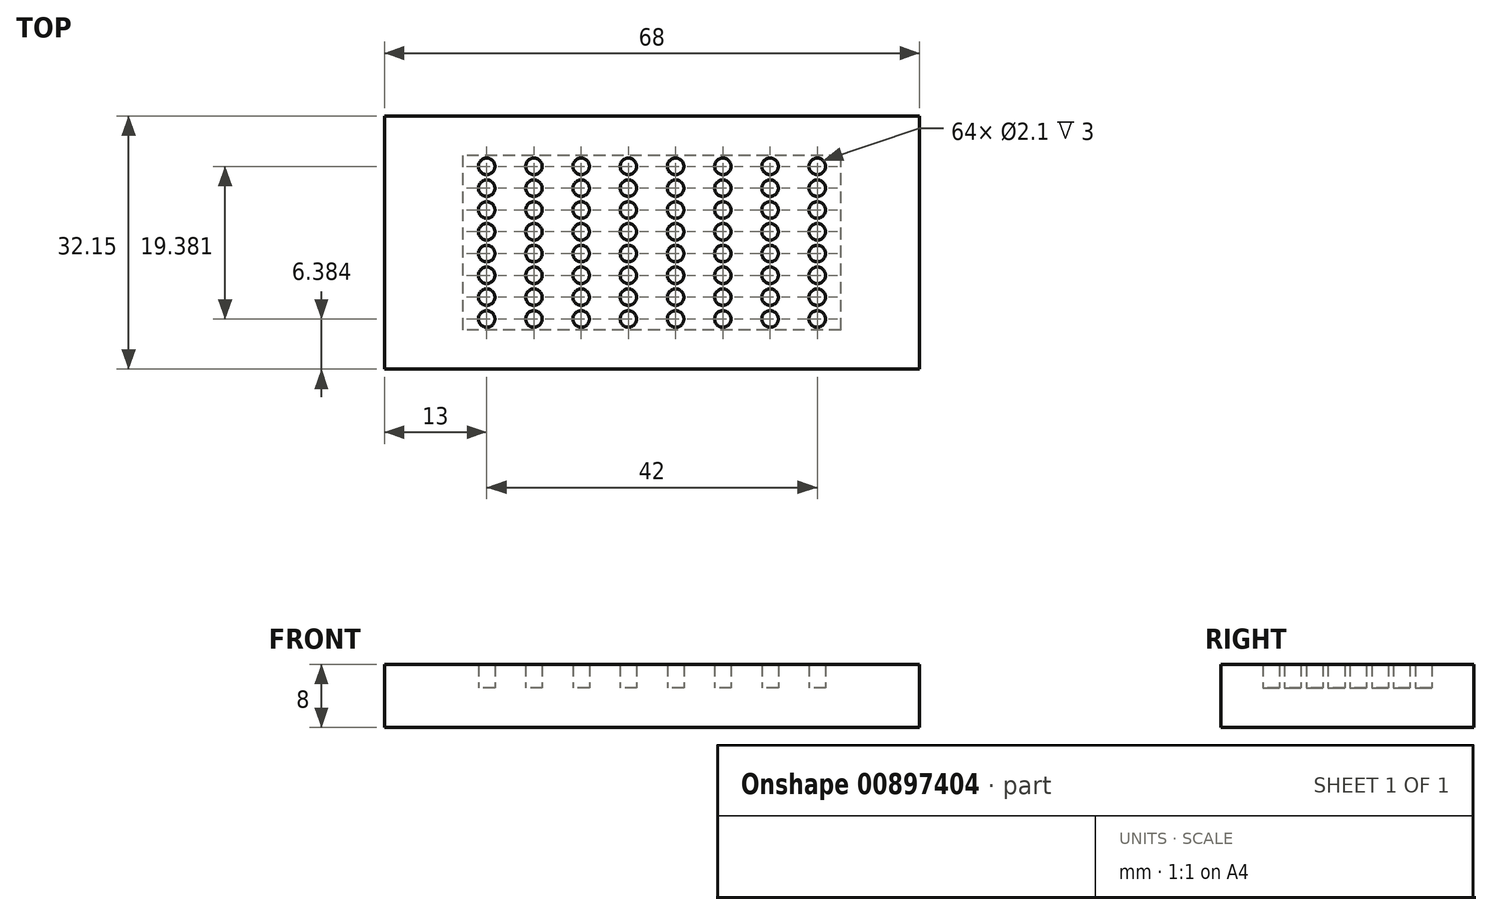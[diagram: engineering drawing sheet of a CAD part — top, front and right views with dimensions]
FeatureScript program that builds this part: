
annotation { "Feature Type Name" : "Feature", "Feature Type Description" : "" }
export const myFeature = defineFeature(function(context is Context, id is Id, definition is map)
    precondition{}
    {
        {
            var Q0;
            Q0=qCreatedBy(makeId("Top.planeOp"),FACE);
            var sketch = newSketch(context, id + "F0", { "sketchPlane" : qUnion([Q0])});
            skLineSegment(sketch, "E0.bottom", {"start": v(0, 0) * mm, "end": v(-48, 0) * mm});
            skLineSegment(sketch, "E0.top", {"start": v(0, 22.15) * mm, "end": v(-48, 22.15) * mm});
            skLineSegment(sketch, "E0.left", {"start": v(0, 0) * mm, "end": v(0, 22.15) * mm});
            skLineSegment(sketch, "E0.right", {"start": v(-48, 0) * mm, "end": v(-48, 22.15) * mm});
            skLineSegment(sketch, "E1.right", {"start": v(51.8, 0) * mm, "end": v(51.8, 10.97) * mm});
            skSolve(sketch);
        }
        {
            var Q0;
            Q0=makeQuery(id+"F0.imprint","IMPRINT",FACE,{"disambiguationData":[TD([[makeQuery(id+"F0.imprint","IMPRINT",EDGE,{"derivedFrom":sQuery(id+"F0.wireOp",EDGE,"E0.bottom")}),-1.0]])]});
            var Q1;
            Q1=makeQuery(id+"F0.imprint","IMPRINT",FACE,{"disambiguationData":[TD([[makeQuery(id+"F0.imprint","IMPRINT",EDGE,{"derivedFrom":sQuery(id+"F0.wireOp",EDGE,"E1.bottom")}),1.0]])]});
            extrude(context, id + "F1", {"entities" : qUnion([Q0, Q1]), "depth" : 4.98 * mm, "offsetDistance" : 25 * mm});
        }
        {
            var Q0;
            Q0=makeQuery(id+"F1.opExtrude","CAP_FACE",FACE,{"disambiguationData":[OSD([sQuery(id+"F0.wireOp",EDGE,"E0.bottom"),sQuery(id+"F0.wireOp",EDGE,"E0.top"),sQuery(id+"F0.wireOp",EDGE,"E0.left"),sQuery(id+"F0.wireOp",EDGE,"E0.right")])],"isStart":false});
            var sketch = newSketch(context, id + "F2", { "sketchPlane" : qUnion([Q0])});
            skCircle(sketch, "E2", {"center": v(-45, 20.77) * mm, "radius": 1.05 * mm});
            skCircle(sketch, "E3", {"center": v(-39, 20.77) * mm, "radius": 1.05 * mm});
            skCircle(sketch, "E4", {"center": v(-33, 20.77) * mm, "radius": 1.05 * mm});
            skCircle(sketch, "E5", {"center": v(-27, 20.77) * mm, "radius": 1.05 * mm});
            skCircle(sketch, "E6", {"center": v(-45, 18) * mm, "radius": 1.05 * mm});
            skCircle(sketch, "E7", {"center": v(-39, 18) * mm, "radius": 1.05 * mm});
            skCircle(sketch, "E8", {"center": v(-33, 18) * mm, "radius": 1.05 * mm});
            skCircle(sketch, "E9", {"center": v(-27, 18) * mm, "radius": 1.05 * mm});
            skCircle(sketch, "E10", {"center": v(-45, 15.23) * mm, "radius": 1.05 * mm});
            skCircle(sketch, "E11", {"center": v(-39, 15.23) * mm, "radius": 1.05 * mm});
            skCircle(sketch, "E12", {"center": v(-33, 15.23) * mm, "radius": 1.05 * mm});
            skCircle(sketch, "E13", {"center": v(-27, 15.23) * mm, "radius": 1.05 * mm});
            skCircle(sketch, "E14", {"center": v(-45, 12.46) * mm, "radius": 1.05 * mm});
            skCircle(sketch, "E15", {"center": v(-39, 12.46) * mm, "radius": 1.05 * mm});
            skCircle(sketch, "E16", {"center": v(-33, 12.46) * mm, "radius": 1.05 * mm});
            skCircle(sketch, "E17", {"center": v(-27, 12.46) * mm, "radius": 1.05 * mm});
            skCircle(sketch, "E18.MirrorC", {"center": v(-3, 20.77) * mm, "radius": 1.05 * mm});
            skCircle(sketch, "E19.MirrorC", {"center": v(-9, 20.77) * mm, "radius": 1.05 * mm});
            skCircle(sketch, "E20.MirrorC", {"center": v(-15, 20.77) * mm, "radius": 1.05 * mm});
            skCircle(sketch, "E21.MirrorC", {"center": v(-21, 20.77) * mm, "radius": 1.05 * mm});
            skCircle(sketch, "E22.MirrorC", {"center": v(-21, 18) * mm, "radius": 1.05 * mm});
            skCircle(sketch, "E23.MirrorC", {"center": v(-15, 18) * mm, "radius": 1.05 * mm});
            skCircle(sketch, "E24.MirrorC", {"center": v(-9, 18) * mm, "radius": 1.05 * mm});
            skCircle(sketch, "E25.MirrorC", {"center": v(-3, 18) * mm, "radius": 1.05 * mm});
            skCircle(sketch, "E26.MirrorC", {"center": v(-3, 15.23) * mm, "radius": 1.05 * mm});
            skCircle(sketch, "E27.MirrorC", {"center": v(-9, 15.23) * mm, "radius": 1.05 * mm});
            skCircle(sketch, "E28.MirrorC", {"center": v(-15, 15.23) * mm, "radius": 1.05 * mm});
            skCircle(sketch, "E29.MirrorC", {"center": v(-21, 15.23) * mm, "radius": 1.05 * mm});
            skCircle(sketch, "E30.MirrorC", {"center": v(-21, 12.46) * mm, "radius": 1.05 * mm});
            skCircle(sketch, "E31.MirrorC", {"center": v(-15, 12.46) * mm, "radius": 1.05 * mm});
            skCircle(sketch, "E32.MirrorC", {"center": v(-9, 12.46) * mm, "radius": 1.05 * mm});
            skCircle(sketch, "E33.MirrorC", {"center": v(-3, 12.46) * mm, "radius": 1.05 * mm});
            skCircle(sketch, "E34.MirrorC", {"center": v(-45, 9.7) * mm, "radius": 1.05 * mm});
            skCircle(sketch, "E35.MirrorC", {"center": v(-45, 6.92) * mm, "radius": 1.05 * mm});
            skCircle(sketch, "E36.MirrorC", {"center": v(-45, 4.15) * mm, "radius": 1.05 * mm});
            skCircle(sketch, "E37.MirrorC", {"center": v(-45, 1.38) * mm, "radius": 1.05 * mm});
            skCircle(sketch, "E38.MirrorC", {"center": v(-39, 1.38) * mm, "radius": 1.05 * mm});
            skCircle(sketch, "E39.MirrorC", {"center": v(-39, 4.15) * mm, "radius": 1.05 * mm});
            skCircle(sketch, "E40.MirrorC", {"center": v(-39, 6.92) * mm, "radius": 1.05 * mm});
            skCircle(sketch, "E41.MirrorC", {"center": v(-39, 9.7) * mm, "radius": 1.05 * mm});
            skCircle(sketch, "E42.MirrorC", {"center": v(-33, 9.7) * mm, "radius": 1.05 * mm});
            skCircle(sketch, "E43.MirrorC", {"center": v(-33, 6.92) * mm, "radius": 1.05 * mm});
            skCircle(sketch, "E44.MirrorC", {"center": v(-33, 4.15) * mm, "radius": 1.05 * mm});
            skCircle(sketch, "E45.MirrorC", {"center": v(-33, 1.38) * mm, "radius": 1.05 * mm});
            skCircle(sketch, "E46.MirrorC", {"center": v(-27, 1.38) * mm, "radius": 1.05 * mm});
            skCircle(sketch, "E47.MirrorC", {"center": v(-27, 4.15) * mm, "radius": 1.05 * mm});
            skCircle(sketch, "E48.MirrorC", {"center": v(-27, 6.92) * mm, "radius": 1.05 * mm});
            skCircle(sketch, "E49.MirrorC", {"center": v(-27, 9.7) * mm, "radius": 1.05 * mm});
            skCircle(sketch, "E50.MirrorC", {"center": v(-21, 9.7) * mm, "radius": 1.05 * mm});
            skCircle(sketch, "E51.MirrorC", {"center": v(-21, 6.92) * mm, "radius": 1.05 * mm});
            skCircle(sketch, "E52.MirrorC", {"center": v(-21, 4.15) * mm, "radius": 1.05 * mm});
            skCircle(sketch, "E53.MirrorC", {"center": v(-21, 1.38) * mm, "radius": 1.05 * mm});
            skCircle(sketch, "E54.MirrorC", {"center": v(-15, 1.38) * mm, "radius": 1.05 * mm});
            skCircle(sketch, "E55.MirrorC", {"center": v(-15, 4.15) * mm, "radius": 1.05 * mm});
            skCircle(sketch, "E56.MirrorC", {"center": v(-15, 6.92) * mm, "radius": 1.05 * mm});
            skCircle(sketch, "E57.MirrorC", {"center": v(-15, 9.7) * mm, "radius": 1.05 * mm});
            skCircle(sketch, "E58.MirrorC", {"center": v(-9, 1.38) * mm, "radius": 1.05 * mm});
            skCircle(sketch, "E59.MirrorC", {"center": v(-9, 4.15) * mm, "radius": 1.05 * mm});
            skCircle(sketch, "E60.MirrorC", {"center": v(-9, 6.92) * mm, "radius": 1.05 * mm});
            skCircle(sketch, "E61.MirrorC", {"center": v(-9, 9.7) * mm, "radius": 1.05 * mm});
            skCircle(sketch, "E62.MirrorC", {"center": v(-3, 9.7) * mm, "radius": 1.05 * mm});
            skCircle(sketch, "E63.MirrorC", {"center": v(-3, 6.92) * mm, "radius": 1.05 * mm});
            skCircle(sketch, "E64.MirrorC", {"center": v(-3, 4.15) * mm, "radius": 1.05 * mm});
            skCircle(sketch, "E65.MirrorC", {"center": v(-3, 1.38) * mm, "radius": 1.05 * mm});
            skLineSegment(sketch, "E66.bottom", {"start": v(-48, 22.15) * mm, "end": v(0, 22.15) * mm});
            skLineSegment(sketch, "E66.top", {"start": v(-48, 0) * mm, "end": v(0, 0) * mm});
            skLineSegment(sketch, "E66.left", {"start": v(-48, 22.15) * mm, "end": v(-48, 0) * mm});
            skLineSegment(sketch, "E66.right", {"start": v(0, 22.15) * mm, "end": v(0, 0) * mm});
            skLineSegment(sketch, "E67.bottom", {"start": v(-58, 27.15) * mm, "end": v(10, 27.15) * mm});
            skLineSegment(sketch, "E67.top", {"start": v(-58, -5) * mm, "end": v(10, -5) * mm});
            skLineSegment(sketch, "E67.left", {"start": v(-58, 27.15) * mm, "end": v(-58, -5) * mm});
            skLineSegment(sketch, "E67.right", {"start": v(10, 27.15) * mm, "end": v(10, -5) * mm});
            skSolve(sketch);
        }
        {
            var Q0;
            Q0=makeQuery(id+"F2.imprint","IMPRINT",FACE,{"disambiguationData":[TD([[makeQuery(id+"F2.imprint","IMPRINT",EDGE,{"derivedFrom":sQuery(id+"F2.wireOp",EDGE,"E2")}),-1.0]])]});
            var Q1;
            Q1=makeQuery(id+"F2.imprint","IMPRINT",FACE,{"disambiguationData":[TD([[makeQuery(id+"F2.imprint","IMPRINT",EDGE,{"derivedFrom":sQuery(id+"F2.wireOp",EDGE,"E66.bottom")}),-1.0]])]});
            extrude(context, id + "F3", {"entities" : qUnion([Q0, Q1]), "depth" : 3 * mm, "offsetDistance" : 25 * mm});
        }
        {
            var Q0;
            Q0=makeQuery(id+"F2.imprint","IMPRINT",FACE,{"disambiguationData":[TD([[makeQuery(id+"F2.imprint","IMPRINT",EDGE,{"derivedFrom":sQuery(id+"F2.wireOp",EDGE,"E66.bottom")}),-1.0]])]});
            extrude(context, id + "F4", {"entities" : qUnion([Q0]), "operationType" : NewBodyOperationType.ADD, "oppositeDirection" : true, "depth" : 5 * mm, "offsetDistance" : 25 * mm});
        }
    });
